annotation { "Feature Type Name" : "Feature", "Feature Type Description" : "" }
export const myFeature = defineFeature(function(context is Context, id is Id, definition is map)
    precondition{}
    {
        {
            var Q0;
            Q0=qCreatedBy(makeId("Front.planeOp"),FACE);
            var sketch = newSketch(context, id + "F0", { "sketchPlane" : qUnion([Q0])});
            skFitSpline(sketch, "E0", {"points": [v(-132.5, -33.16) * mm, v(-7.92, 13.83) * mm, v(-127.13, 65.65) * mm, v(-132.5, -33.16) * mm]});
            skSolve(sketch);
        }
        {
            var Q0;
            Q0=makeQuery(id+"F0.imprint","IMPRINT",FACE,{"disambiguationData":[TD([[makeQuery(id+"F0.imprint","IMPRINT",EDGE,{"derivedFrom":sQuery(id+"F0.wireOp",EDGE,"E0")}),1.0]])]});
            extrude(context, id + "F1", {"entities" : qUnion([Q0]), "depth" : 254 * mm, "offsetDistance" : 25.4 * mm});
        }
        {
            var Q0;
            Q0=qCreatedBy(makeId("Front.planeOp"),FACE);
            var sketch = newSketch(context, id + "F2", { "sketchPlane" : qUnion([Q0])});
            skLineSegment(sketch, "E1", {"start": v(0, 295.1) * mm, "end": v(37.56, 177.57) * mm});
            skLineSegment(sketch, "E2", {"start": v(0, 236.33) * mm, "end": v(0, 0) * mm});
            skPoint(sketch, "E2.startSnap0", {"position": v(18.78, 236.33) * mm});
            skLineSegment(sketch, "E3", {"start": v(0, 0) * mm, "end": v(37.56, 177.57) * mm});
            skLineSegment(sketch, "E4", {"start": v(0, 236.33) * mm, "end": v(0, 295.1) * mm});
            skLineSegment(sketch, "E5", {"start": v(0, 295.1) * mm, "end": v(-133.61, 155.45) * mm});
            skLineSegment(sketch, "E6", {"start": v(-133.61, 155.45) * mm, "end": v(0, 0) * mm});
            skLineSegment(sketch, "E7", {"start": v(0, 236.33) * mm, "end": v(-131.67, 153.2) * mm});
            skLineSegment(sketch, "E8", {"start": v(-131.67, 153.2) * mm, "end": v(37.56, 177.57) * mm});
            skLineSegment(sketch, "E9", {"start": v(0, 236.33) * mm, "end": v(18.78, 236.33) * mm});
            skLineSegment(sketch, "E10", {"start": v(18.78, 236.33) * mm, "end": v(0, 0) * mm});
            skLineSegment(sketch, "E11", {"start": v(0, 295.1) * mm, "end": v(-67.1, 162.5) * mm});
            skLineSegment(sketch, "E12", {"start": v(-67.1, 162.5) * mm, "end": v(-2.82, 129.96) * mm});
            skLineSegment(sketch, "E13", {"start": v(-2.82, 126.79) * mm, "end": v(-9.09, 129.96) * mm});
            skLineSegment(sketch, "E14", {"start": v(-9.09, 129.96) * mm, "end": v(-47.7, 117.62) * mm});
            skLineSegment(sketch, "E15", {"start": v(-47.7, 117.62) * mm, "end": v(-67.1, 162.5) * mm});
            skLineSegment(sketch, "E16", {"start": v(-2.82, 126.79) * mm, "end": v(-2.82, 129.96) * mm});
            skLineSegment(sketch, "E17", {"start": v(37.56, 177.57) * mm, "end": v(0, 236.33) * mm});
            skLineSegment(sketch, "E18", {"start": v(-67.1, 162.5) * mm, "end": v(-128.1, 155.45) * mm});
            skLineSegment(sketch, "E19", {"start": v(-128.1, 155.45) * mm, "end": v(-2.82, 129.96) * mm});
            skSolve(sketch);
        }
        {
            var Q0;
            Q0 = qSketchRegion(id + "F2", true);
            extrude(context, id + "F3", {"entities" : qUnion([Q0]), "operationType" : NewBodyOperationType.ADD, "depth" : 98.3 * mm, "offsetDistance" : 25.4 * mm});
        }
        {
            var Q0;
            Q0=qCreatedBy(makeId("Front.planeOp"),FACE);
            var sketch = newSketch(context, id + "F4", { "sketchPlane" : qUnion([Q0])});
            skLineSegment(sketch, "E20", {"start": v(133.1, 421.14) * mm, "end": v(59.19, 421.14) * mm});
            skLineSegment(sketch, "E21", {"start": v(137.03, 439.46) * mm, "end": v(133.1, 372.73) * mm});
            skLineSegment(sketch, "E22", {"start": v(106.94, 336.76) * mm, "end": v(44.8, 336.76) * mm});
            skLineSegment(sketch, "E23", {"start": v(106.94, 336.76) * mm, "end": v(136.37, 336.76) * mm});
            skLineSegment(sketch, "E24", {"start": v(136.37, 336.76) * mm, "end": v(106.94, 336.76) * mm});
            skLineSegment(sketch, "E25", {"start": v(106.94, 336.76) * mm, "end": v(106.94, 294.9) * mm});
            skLineSegment(sketch, "E26", {"start": v(136.37, 294.9) * mm, "end": v(42.18, 294.9) * mm});
            skLineSegment(sketch, "E27", {"start": v(126.56, 253.68) * mm, "end": v(50.68, 253.68) * mm});
            skLineSegment(sketch, "E28", {"start": v(50.68, 228.83) * mm, "end": v(50.68, 253.68) * mm});
            skLineSegment(sketch, "E29", {"start": v(126.56, 253.68) * mm, "end": v(126.56, 198.74) * mm});
            skLineSegment(sketch, "E30", {"start": v(126.56, 198.74) * mm, "end": v(126.56, 253.68) * mm});
            skLineSegment(sketch, "E31", {"start": v(88.62, 253.68) * mm, "end": v(88.62, 211.82) * mm});
            skCircle(sketch, "E32", {"center": v(108.25, 65.3) * mm, "radius": 45.8 * mm});
            skLineSegment(sketch, "E33", {"start": v(131.8, -26.94) * mm, "end": v(55.92, -26.94) * mm});
            skLineSegment(sketch, "E34", {"start": v(86, -26.94) * mm, "end": v(86, -74.04) * mm});
            skLineSegment(sketch, "E35", {"start": v(55.92, -26.94) * mm, "end": v(55.92, -41.98) * mm});
            skLineSegment(sketch, "E36", {"start": v(131.8, -26.94) * mm, "end": v(131.8, -74.04) * mm});
            skLineSegment(sketch, "E37", {"start": v(55.92, -41.98) * mm, "end": v(55.92, -75.34) * mm});
            skLineSegment(sketch, "E38", {"start": v(55.92, -75.34) * mm, "end": v(86, -74.04) * mm});
            skLineSegment(sketch, "E39", {"start": v(-26.5, 430.95) * mm, "end": v(-152.1, 430.95) * mm});
            skLineSegment(sketch, "E40.bottom", {"start": v(-54.6, 425.73) * mm, "end": v(-88.7, 425.73) * mm});
            skLineSegment(sketch, "E40.top", {"start": v(-54.6, 373.24) * mm, "end": v(-88.7, 373.24) * mm});
            skLineSegment(sketch, "E40.left", {"start": v(-54.6, 425.73) * mm, "end": v(-54.6, 373.24) * mm});
            skLineSegment(sketch, "E40.right", {"start": v(-88.7, 425.73) * mm, "end": v(-88.7, 373.24) * mm});
            skLineSegment(sketch, "E41.bottom", {"start": v(-100.51, 425.73) * mm, "end": v(-132, 425.73) * mm});
            skLineSegment(sketch, "E41.top", {"start": v(-100.51, 373.24) * mm, "end": v(-132, 373.24) * mm});
            skLineSegment(sketch, "E41.left", {"start": v(-100.51, 425.73) * mm, "end": v(-100.51, 373.24) * mm});
            skLineSegment(sketch, "E41.right", {"start": v(-132, 425.73) * mm, "end": v(-132, 373.24) * mm});
            skLineSegment(sketch, "E42", {"start": v(-69.03, 277.47) * mm, "end": v(-141.19, 277.47) * mm});
            skCircle(sketch, "E43", {"center": v(-93.95, 299.11) * mm, "radius": 25.07 * mm});
            skLineSegment(sketch, "E44", {"start": v(-88.7, 211.2) * mm, "end": v(-88.7, 241.38) * mm});
            skLineSegment(sketch, "E45", {"start": v(-88.7, 241.38) * mm, "end": v(-151.03, 241.38) * mm});
            skLineSegment(sketch, "E46", {"start": v(-151.03, 242.04) * mm, "end": v(-151.03, 205.3) * mm});
            skCircle(sketch, "E47", {"center": v(-141.19, 129.2) * mm, "radius": 48.4 * mm});
            skLineSegment(sketch, "E48", {"start": v(-201.54, 23.59) * mm, "end": v(-159.56, 23.59) * mm});
            skLineSegment(sketch, "E49", {"start": v(-159.56, 23.59) * mm, "end": v(-191.7, 0) * mm});
            skLineSegment(sketch, "E50", {"start": v(-191.7, 0) * mm, "end": v(-159.56, 0) * mm});
            skLineSegment(sketch, "E51", {"start": v(-427.1, 310.17) * mm, "end": v(-411.66, 129.4) * mm});
            skLineSegment(sketch, "E52", {"start": v(-420.12, 228.47) * mm, "end": v(-388.95, 266.57) * mm});
            skLineSegment(sketch, "E53", {"start": v(-309.91, 334.7) * mm, "end": v(-323.54, 367.4) * mm});
            skLineSegment(sketch, "E54", {"start": v(-323.54, 367.4) * mm, "end": v(-361.06, 364.2) * mm});
            skLineSegment(sketch, "E55", {"start": v(-361.06, 364.2) * mm, "end": v(-354.43, 337.43) * mm});
            skLineSegment(sketch, "E56", {"start": v(-354.43, 337.43) * mm, "end": v(-353.52, 323.8) * mm});
            skLineSegment(sketch, "E57", {"start": v(-353.52, 323.8) * mm, "end": v(-229.06, 205.7) * mm});
            skLineSegment(sketch, "E58", {"start": v(-229.06, 205.7) * mm, "end": v(-497.05, 149.38) * mm});
            skLineSegment(sketch, "E59", {"start": v(-497.05, 149.38) * mm, "end": v(-290.84, 240.22) * mm});
            skLineSegment(sketch, "E60", {"start": v(-290.84, 240.22) * mm, "end": v(-402.58, 361.96) * mm});
            skLineSegment(sketch, "E61", {"start": v(-402.58, 361.96) * mm, "end": v(-427.1, 310.17) * mm});
            skLineSegment(sketch, "E62", {"start": v(-405.3, 129.4) * mm, "end": v(-290.84, 240.22) * mm});
            skSolve(sketch);
        }
        {
            var Q0;
            Q0=makeQuery(id+"F4.imprint","IMPRINT",FACE,{"disambiguationData":[TD([[makeQuery(id+"F4.imprint","IMPRINT",EDGE,{"derivedFrom":sQuery(id+"F4.wireOp",EDGE,"E32")}),1.0]])]});
            var Q1;
            {var subQ1=sQuery(id+"F4.wireOp",EDGE,"E34");Q1=makeQuery(id+"F4.imprint","IMPRINT",FACE,{"disambiguationData":[TD([[makeQuery(id+"F4.imprint","IMPRINT",EDGE,{"derivedFrom":subQ1}),-1.0]])]});}
            var Q2;
            Q2=makeQuery(id+"F4.imprint","IMPRINT",FACE,{"disambiguationData":[TD([[makeQuery(id+"F4.imprint","IMPRINT",EDGE,{"derivedFrom":sQuery(id+"F4.wireOp",EDGE,"E40.bottom")}),1.0]])]});
            var Q3;
            Q3=makeQuery(id+"F4.imprint","IMPRINT",FACE,{"disambiguationData":[TD([[makeQuery(id+"F4.imprint","IMPRINT",EDGE,{"derivedFrom":sQuery(id+"F4.wireOp",EDGE,"E41.bottom")}),1.0]])]});
            var Q4;
            Q4=makeQuery(id+"F4.imprint","IMPRINT",FACE,{"disambiguationData":[TD([[makeQuery(id+"F4.imprint","IMPRINT",EDGE,{"derivedFrom":sQuery(id+"F4.wireOp",EDGE,"E47")}),1.0]])]});
            var Q5;
            {var subQ0=sQuery(id+"F4.wireOp",EDGE,"E43");var subQ1=sQuery(id+"F4.wireOp",EDGE,"E42");var subQ2=makeQuery(id+"F4.imprint","INTERSECT",VERTEX,{"disambiguationData":[OD(0.0)],"derivedFrom":[subQ1,subQ0]});Q5=makeQuery(id+"F4.imprint","IMPRINT",FACE,{"disambiguationData":[TD([[makeQuery(id+"F4.imprint","IMPRINT",EDGE,{"disambiguationData":[TD([[subQ2,1.0]])],"derivedFrom":subQ1}),1.0]])]});}
            var Q6;
            {var subQ0=sQuery(id+"F4.wireOp",EDGE,"E43");var subQ1=sQuery(id+"F4.wireOp",EDGE,"E42");var subQ2=makeQuery(id+"F4.imprint","INTERSECT",VERTEX,{"disambiguationData":[OD(0.0)],"derivedFrom":[subQ1,subQ0]});Q6=makeQuery(id+"F4.imprint","IMPRINT",FACE,{"disambiguationData":[TD([[makeQuery(id+"F4.imprint","IMPRINT",EDGE,{"disambiguationData":[TD([[subQ2,1.0]])],"derivedFrom":subQ1}),-1.0]])]});}
            var Q7;
            {var subQ0=sQuery(id+"F4.wireOp",EDGE,"E58");var subQ1=sQuery(id+"F4.wireOp",EDGE,"E51");var subQ2=makeQuery(id+"F4.imprint","INTERSECT",VERTEX,{"derivedFrom":[subQ1,subQ0]});Q7=makeQuery(id+"F4.imprint","IMPRINT",FACE,{"disambiguationData":[TD([[makeQuery(id+"F4.imprint","IMPRINT",EDGE,{"disambiguationData":[TD([[subQ2,1.0]])],"derivedFrom":subQ1}),-1.0]])]});}
            var Q8;
            {var subQ0=sQuery(id+"F4.wireOp",EDGE,"E58");var subQ1=sQuery(id+"F4.wireOp",EDGE,"E51");var subQ2=makeQuery(id+"F4.imprint","INTERSECT",VERTEX,{"derivedFrom":[subQ1,subQ0]});Q8=makeQuery(id+"F4.imprint","IMPRINT",FACE,{"disambiguationData":[TD([[makeQuery(id+"F4.imprint","IMPRINT",EDGE,{"disambiguationData":[TD([[subQ2,1.0]])],"derivedFrom":subQ1}),1.0]])]});}
            extrude(context, id + "F5", {"entities" : qUnion([Q0, Q1, Q2, Q3, Q4, Q5, Q6, Q7, Q8]), "operationType" : NewBodyOperationType.ADD, "depth" : 254000 * mm, "offsetDistance" : 25.4 * mm});
        }
    });